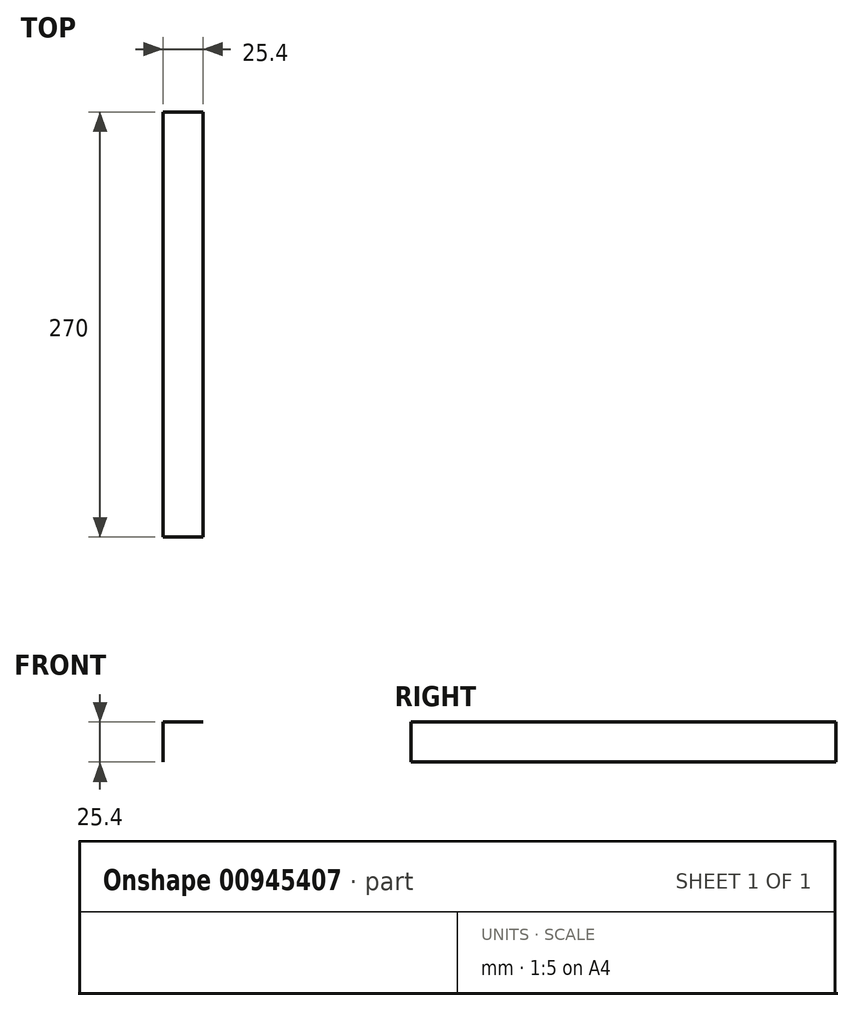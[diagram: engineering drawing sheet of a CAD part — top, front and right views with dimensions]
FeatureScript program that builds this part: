
annotation { "Feature Type Name" : "Feature", "Feature Type Description" : "" }
export const myFeature = defineFeature(function(context is Context, id is Id, definition is map)
    precondition{}
    {
        {
            var Q0;
            Q0=qCreatedBy(makeId("Front.planeOp"),FACE);
            var sketch = newSketch(context, id + "F0", { "sketchPlane" : qUnion([Q0])});
            skLineSegment(sketch, "E0.bottom", {"start": v(17.65, -21.22) * mm, "end": v(43.05, -21.22) * mm});
            skLineSegment(sketch, "E0.left", {"start": v(17.65, -21.22) * mm, "end": v(17.65, -46.62) * mm});
            skSolve(sketch);
        }
        {
            var Q0;
            Q0=sQuery(id+"F0.wireOp",EDGE,"E0.bottom");
            var Q1;
            Q1=sQuery(id+"F0.wireOp",EDGE,"E0.left");
            extrude(context, id + "F1", {"bodyType" : ToolBodyType.SURFACE, "surfaceEntities" : qUnion([Q0, Q1]), "depth" : 270 * mm, "offsetDistance" : 25.4 * mm});
        }
    });
